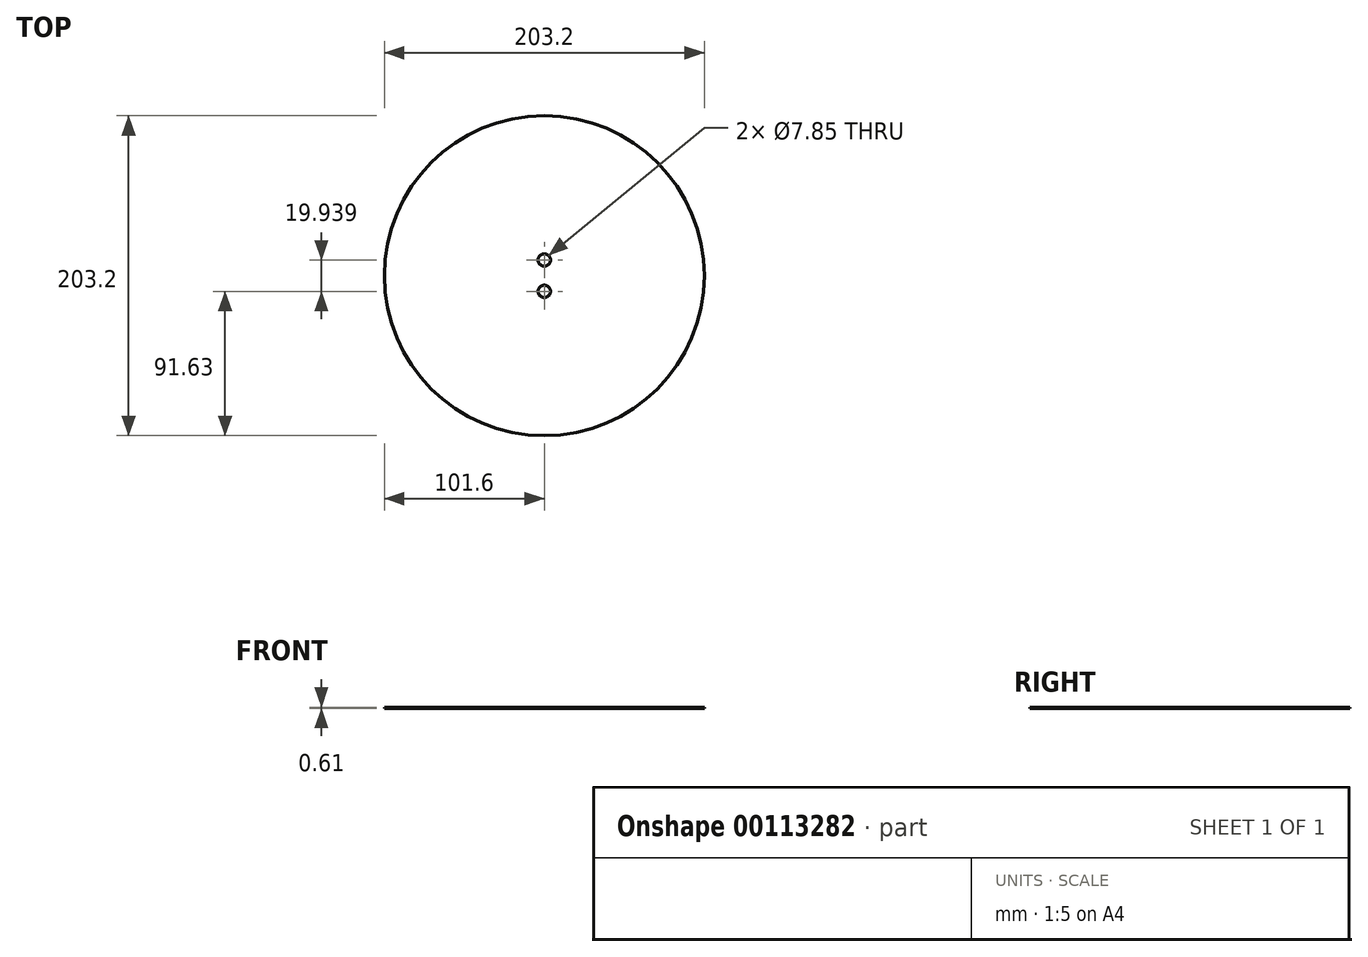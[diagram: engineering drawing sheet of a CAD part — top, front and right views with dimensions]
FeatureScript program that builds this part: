
annotation { "Feature Type Name" : "Feature", "Feature Type Description" : "" }
export const myFeature = defineFeature(function(context is Context, id is Id, definition is map)
    precondition{}
    {
        {
            var Q0;
            Q0=qCreatedBy(makeId("Top.planeOp"),FACE);
            var sketch = newSketch(context, id + "F0", { "sketchPlane" : qUnion([Q0])});
            skCircle(sketch, "E0", {"center": v(0, 0) * mm, "radius": 101.6 * mm});
            skCircle(sketch, "E1", {"center": v(0, 9.97) * mm, "radius": 3.92 * mm});
            skCircle(sketch, "E2", {"center": v(0, -9.97) * mm, "radius": 3.92 * mm});
            skLineSegment(sketch, "E3", {"start": v(0, 9.97) * mm, "end": v(0, -9.97) * mm, "construction": true});
            skSolve(sketch);
        }
        {
            var Q0;
            Q0 = qSketchRegion(id + "F0", true);
            extrude(context, id + "F1", {"entities" : qUnion([Q0]), "depth" : 0.6 * mm});
        }
    });
